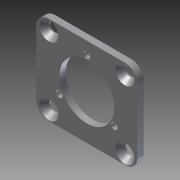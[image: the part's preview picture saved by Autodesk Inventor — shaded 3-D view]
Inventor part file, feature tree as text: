
AUTODESK INVENTOR PART (.ipt)
format: ipt  version: 2012 (Build 160160000, 160)  size: 139,264 bytes
history: native  units: in
note: dims shown in document units (in); Inventor stores cm internally (conversion verified against a paired STEP export)
features: extrude x2, sketch x1, hole x1, fillet x1
ambient origin geometry x8: Origin, YZ Plane, XZ Plane, XY Plane, X Axis, Y Axis, Z Axis, Center Point
bodies: Solid1 (feature_tree)
feature tree (5):
  sketch  "Sketch1"  dims[d0=1.75in d1=2.5in d2=1.25in d3=0.875in d4=1.08in d7=0.1275in d9=0.625in d13=1.1811in d15=360.0deg d17=1.7in d18=0.2in d19=0.2in d20=0.75in d21=0.75in d22=0.125in d23=0.0in d24=0.1935in d25=0.75in d26=0.375in d27=0.25in d28=0.5635in d29=1.0in d30=0.8108in d31=1.35in d32=1.5in d35=60.0deg d36=0.25in d37=0.25in d38=1.0in d39=0.0in d40=0.25in]
  extrude  "Extrusion1"  Depth=2.5in
  hole  "Hole1"  [1 undecoded]
  extrude  "Extrusion2"  Depth=0.875in
  fillet  "Fillet1"  Radius=1.08in
note: 1 required parameter value undecoded (feature->parameter linkage not recoverable at this tier; creation-order binding heuristic only, values carry confidence <= 0.55)
